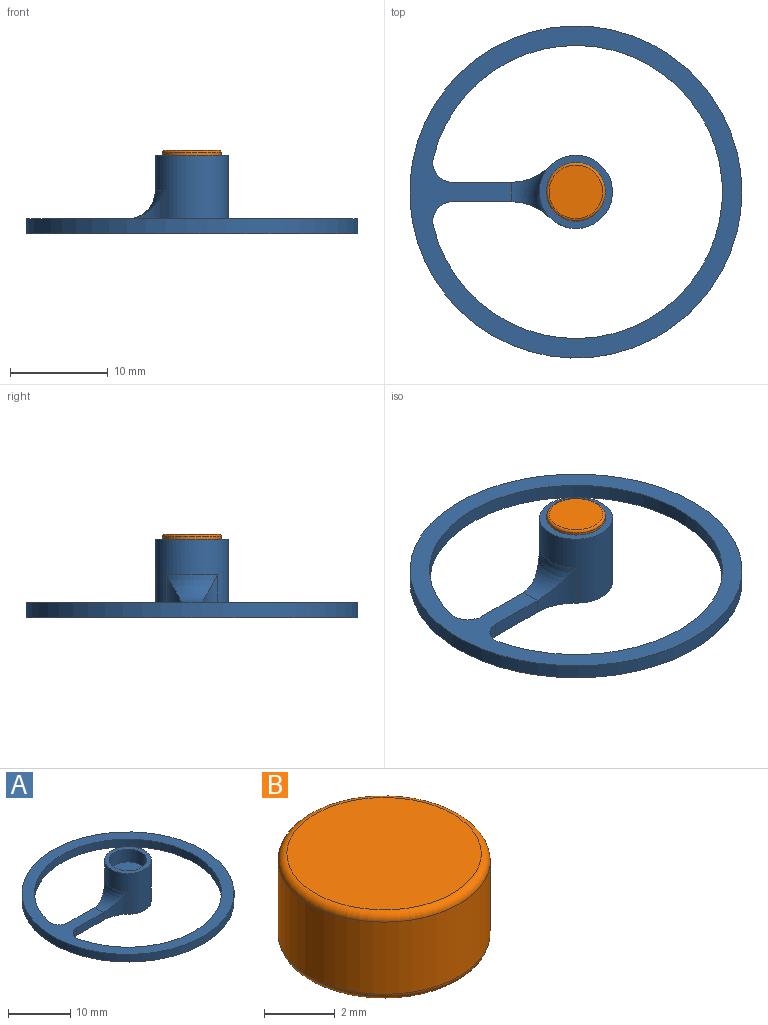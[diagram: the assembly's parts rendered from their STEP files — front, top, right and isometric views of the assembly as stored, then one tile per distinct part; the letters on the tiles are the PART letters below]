
ASSEMBLY  parts=2 mates=1
PART A: 15 faces, bbox 34x34x8 mm
  f0: plane 6.01x1.5mm, normal (0,1,0), area 9mm2, adj f4,f8,f9,f14
  f1: plane 6.01x1.5mm, normal (0,-1,0), area 9mm2, adj f5,f8,f9,f13
  f2: cylinder r=15mm len=30mm, axis (0,0,-1), area 130.9mm2, adj f8,f9,f13,f14
  f3: plane 7.5x7.5mm, normal (0,0,1), area 15.9mm2, adj f6,f11
  f4: cylinder r=5.64mm len=4.39mm, axis (0,0,-1), area 11mm2, adj f0,f6,f8,f9,f10
  f5: cylinder r=5.64mm len=4.39mm, axis (0,0,-1), area 11mm2, adj f1,f6,f8,f9,f10
  f6: cylinder r=3.75mm len=8mm, axis (0,0,-1), area 162.6mm2, adj f3,f4,f5,f9,f10
  f7: cylinder r=17mm len=34mm, axis (0,0,-1), area 160.2mm2, adj f8,f9
  f8: plane 34x34mm, normal (0,0,1), area 220.4mm2, adj f0,f1,f2,f4,f5,f7,f10,f13
  f9: plane 34x34mm, normal (0,0,-1), area 272.6mm2, adj f0,f1,f2,f4,f5,f6,f7,f13
  f10: torus R=6.64mm, axis (0,0,-1), area 15.1mm2, adj f4,f5,f6,f8
  f11: cylinder r=3mm len=6mm, axis (0,0,1), area 47.1mm2, adj f3,f12
  f12: plane 6x6mm, normal (0,0,1), area 28.3mm2, adj f11
  f13: cylinder r=2mm len=2.46mm, axis (0,0,-1), area 5.4mm2, adj f1,f2,f8,f9
  f14: cylinder r=2mm len=2.46mm, axis (0,0,-1), area 5.4mm2, adj f0,f2,f8,f9
PART B: 5 faces, bbox 6.5x6.5x3 mm
  f0: cylinder r=3mm len=6mm, axis (0,0,-1), area 47.1mm2, adj f3,f4
  f1: plane 5.5x5.5mm, normal (0,0,1), area 23.8mm2, adj f4
  f2: plane 5.5x5.5mm, normal (0,0,-1), area 23.8mm2, adj f3
  f3: torus R=2.75mm, axis (0,0,1), area 7.2mm2, adj f0,f2
  f4: torus R=2.75mm, axis (0,0,1), area 7.2mm2, adj f0,f1
PLACE A rot(axis=(0.17,0.52,0.84),0deg) t=(-2.21,-0.52,2.41)mm
PLACE B rot(axis=(-1,0,0),180deg) t=(-2.21,-0.52,10.91)mm
MATE fastened A.f11 <-> B.f0  axis (0,0,1) through (-2.21,-0.52,7.91)mm
